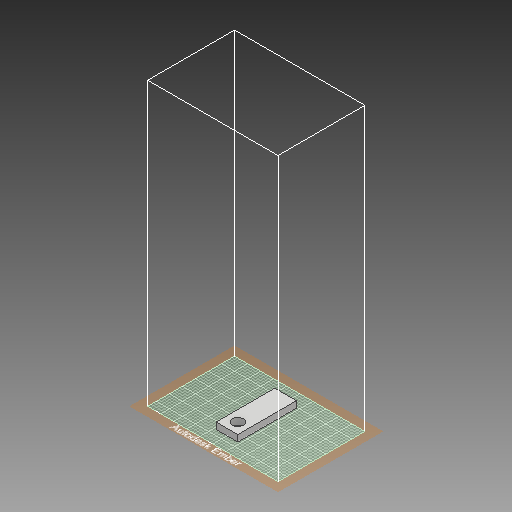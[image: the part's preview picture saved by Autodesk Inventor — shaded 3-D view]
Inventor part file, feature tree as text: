
AUTODESK INVENTOR PART (.ipt)
format: ipt  version: 2018 (Build 220112000, 112)  size: 263,680 bytes
history: native  units: mm
features: extrude x6, sketch x6
ambient origin geometry x8: Origin, YZ Plane, XZ Plane, XY Plane, X Axis, Y Axis, Z Axis, Center Point
bodies: Solid1 (feature_tree)
feature tree (12):
  extrude  "Extrusion1"  Depth=27.0mm
  extrude  "Extrusion2"  Depth=10.0mm
  extrude  "Extrusion4"  Depth=10.0mm TaperAngle=0.0deg
  extrude  "Extrusion5"  Depth=27.0mm TaperAngle=0.0deg
  extrude  "Extrusion6"  Depth=15.0mm
  extrude  "Extrusion7"  Depth=3.0mm TaperAngle=0.0deg
  sketch  "Sketch1"  dims[d0=10.0mm d1=27.0mm]
  sketch  "Sketch2"  dims[d2=10.0mm d3=0.0mm d4=5.0mm]
  sketch  "Sketch4"  dims[d5=5.1mm d6=10.0mm d7=0.0mm]
  sketch  "Sketch5"  dims[d13=27.0mm d14=7.0mm d15=0.0mm]
  sketch  "Sketch6"  dims[d16=22.5mm d17=15.0mm]
  sketch  "Sketch7"  dims[d18=22.5mm d19=3.0mm d20=0.0mm d21=15.0mm d22=15.0mm d23=25.0mm d24=0.0mm d25=15.0mm d26=15.0mm d27=3.5mm d28=3.5mm d29=25.0mm d30=0.0mm]
